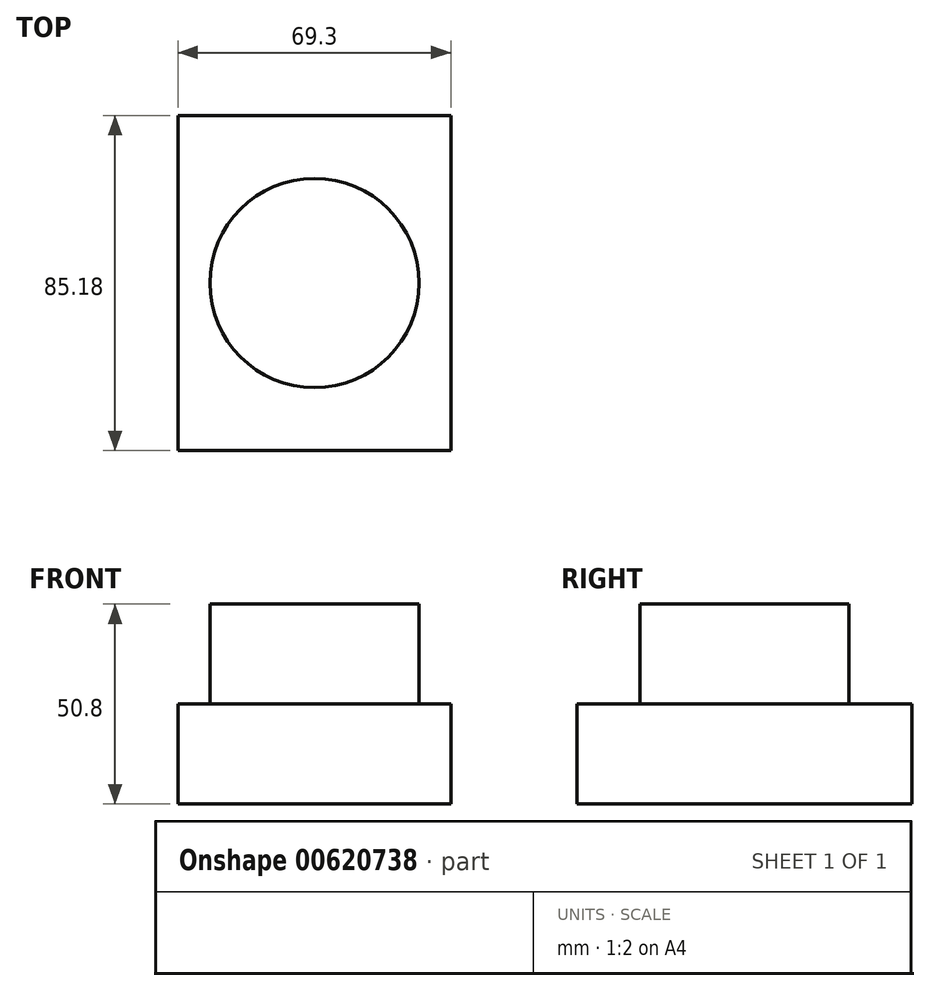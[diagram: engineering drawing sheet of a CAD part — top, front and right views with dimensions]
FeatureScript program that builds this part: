
annotation { "Feature Type Name" : "Feature", "Feature Type Description" : "" }
export const myFeature = defineFeature(function(context is Context, id is Id, definition is map)
    precondition{}
    {
        {
            var Q0;
            Q0=qCreatedBy(makeId("Top.planeOp"),FACE);
            var sketch = newSketch(context, id + "F0", { "sketchPlane" : qUnion([Q0])});
            skLineSegment(sketch, "E0.bottom", {"start": v(34.65, -42.59) * mm, "end": v(-34.65, -42.59) * mm});
            skLineSegment(sketch, "E0.top", {"start": v(34.65, 42.59) * mm, "end": v(-34.65, 42.59) * mm});
            skLineSegment(sketch, "E0.left", {"start": v(34.65, -42.59) * mm, "end": v(34.65, 42.59) * mm});
            skLineSegment(sketch, "E0.right", {"start": v(-34.65, -42.59) * mm, "end": v(-34.65, 42.59) * mm});
            skPoint(sketch, "E0.middle", {"position": v(0, 0) * mm});
            skSolve(sketch);
        }
        {
            var Q0;
            Q0=makeQuery(id+"F0.imprint","IMPRINT",FACE,{"disambiguationData":[TD([[makeQuery(id+"F0.imprint","IMPRINT",EDGE,{"derivedFrom":sQuery(id+"F0.wireOp",EDGE,"E0.bottom")}),-1.0]])]});
            extrude(context, id + "F1", {"entities" : qUnion([Q0]), "depth" : 25.4 * mm, "offsetDistance" : 25.4 * mm});
        }
        {
            var Q0;
            Q0=makeQuery(id+"F1.opExtrude","CAP_FACE",FACE,{"disambiguationData":[OSD([sQuery(id+"F0.wireOp",EDGE,"E0.bottom"),sQuery(id+"F0.wireOp",EDGE,"E0.top"),sQuery(id+"F0.wireOp",EDGE,"E0.left"),sQuery(id+"F0.wireOp",EDGE,"E0.right")])],"isStart":false});
            var sketch = newSketch(context, id + "F2", { "sketchPlane" : qUnion([Q0])});
            skSolve(sketch);
        }
        {
            var Q0;
            Q0=makeQuery(id+"F2.imprint","IMPRINT",FACE,{"disambiguationData":[TD([[makeQuery(id+"F2.imprint","IMPRINT",EDGE,{"derivedFrom":makeQuery(id+"F1.opExtrude","CAP_EDGE",EDGE,{"disambiguationData":[OSD([sQuery(id+"F0.wireOp",EDGE,"E0.bottom")])],"isStart":false})}),-1.0]])]});
            var sketch = newSketch(context, id + "F3", { "sketchPlane" : qUnion([Q0])});
            skCircle(sketch, "E1", {"center": v(0, 0) * mm, "radius": 26.58 * mm});
            skSolve(sketch);
        }
        {
            var Q0;
            Q0 = qSketchRegion(id + "F3", true);
            extrude(context, id + "F4", {"entities" : qUnion([Q0]), "operationType" : NewBodyOperationType.ADD, "depth" : 25.4 * mm, "offsetDistance" : 25.4 * mm});
        }
    });
